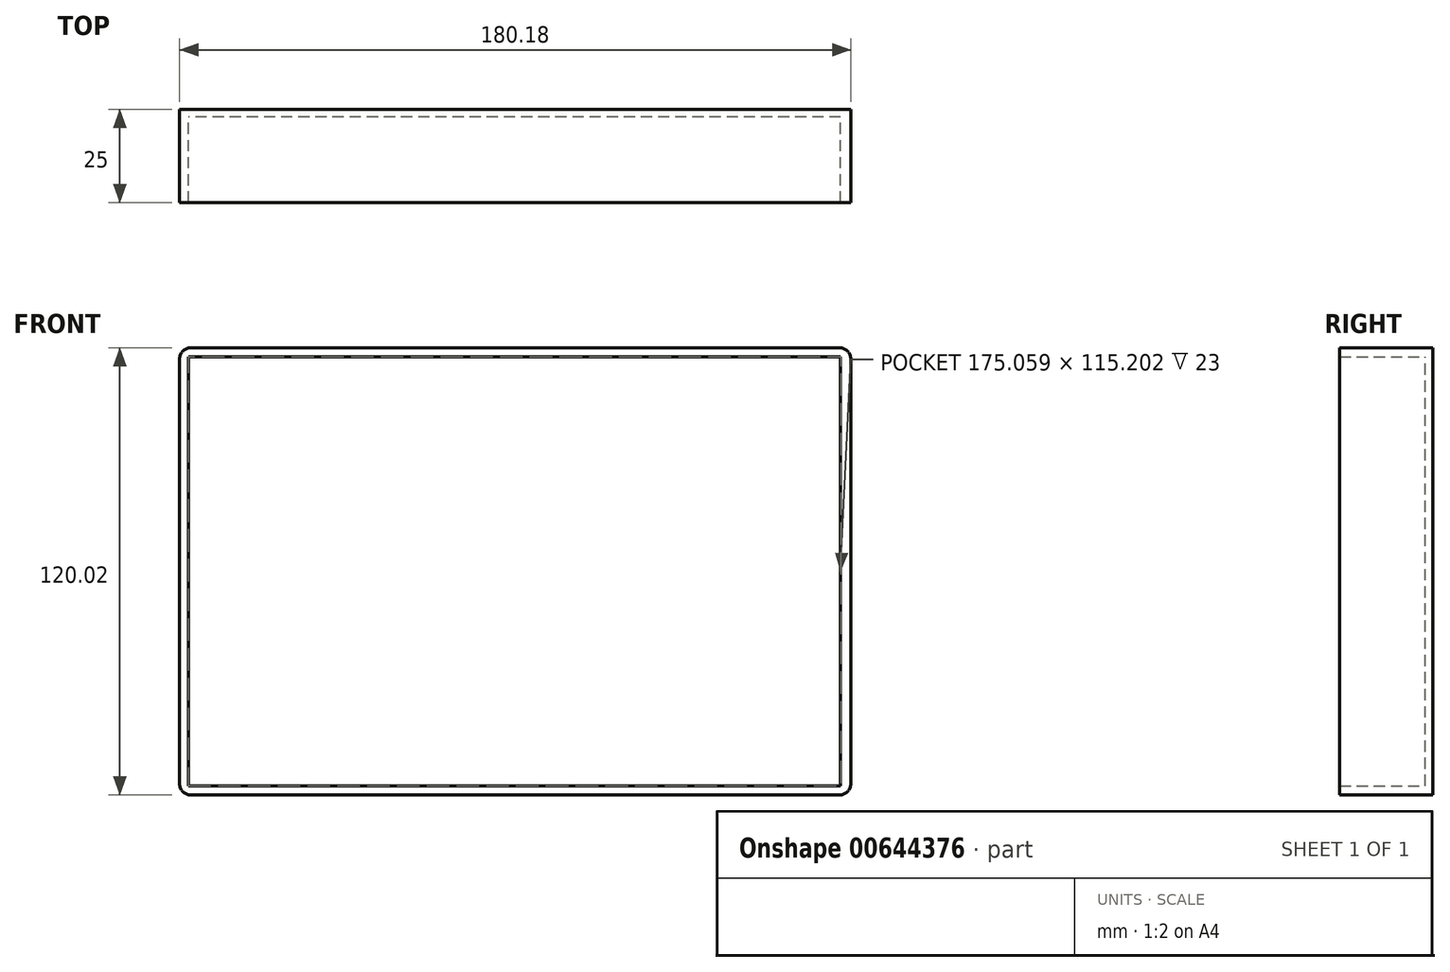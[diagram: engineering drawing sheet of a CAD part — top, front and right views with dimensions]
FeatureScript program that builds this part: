
annotation { "Feature Type Name" : "Feature", "Feature Type Description" : "" }
export const myFeature = defineFeature(function(context is Context, id is Id, definition is map)
    precondition{}
    {
        {
            var Q0;
            Q0=qCreatedBy(makeId("Front.planeOp"),FACE);
            var sketch = newSketch(context, id + "F0", { "sketchPlane" : qUnion([Q0])});
            skLineSegment(sketch, "E0.bottom", {"start": v(90.09, 60) * mm, "end": v(-90.09, 60) * mm});
            skLineSegment(sketch, "E0.top", {"start": v(90.09, -60) * mm, "end": v(-90.09, -60) * mm});
            skLineSegment(sketch, "E0.left", {"start": v(90.09, 60) * mm, "end": v(90.09, -60) * mm});
            skLineSegment(sketch, "E0.right", {"start": v(-90.09, 60) * mm, "end": v(-90.09, -60) * mm});
            skPoint(sketch, "E0.middle", {"position": v(0, 0) * mm});
            skLineSegment(sketch, "E1", {"start": v(-87.68, 57.6) * mm, "end": v(87.38, 57.6) * mm});
            skLineSegment(sketch, "E2", {"start": v(87.38, 57.6) * mm, "end": v(87.38, -57.6) * mm});
            skLineSegment(sketch, "E3", {"start": v(87.38, -57.6) * mm, "end": v(-87.68, -57.6) * mm});
            skLineSegment(sketch, "E4", {"start": v(-87.68, -57.6) * mm, "end": v(-87.68, 57.6) * mm});
            skLineSegment(sketch, "E5", {"start": v(-90.09, 60) * mm, "end": v(-87.68, 57.6) * mm});
            skLineSegment(sketch, "E6", {"start": v(0, 60) * mm, "end": v(0, 57.6) * mm});
            skPoint(sketch, "E6.endSnap0", {"position": v(-0.15, 57.6) * mm});
            skLineSegment(sketch, "E7", {"start": v(90.09, 60) * mm, "end": v(87.38, 57.6) * mm});
            skLineSegment(sketch, "E8", {"start": v(-90.09, 0) * mm, "end": v(-87.68, 0) * mm});
            skLineSegment(sketch, "E9", {"start": v(-87.68, -57.6) * mm, "end": v(-90.09, -60) * mm});
            skLineSegment(sketch, "E10", {"start": v(-0.15, -57.6) * mm, "end": v(-0.15, -60) * mm});
            skLineSegment(sketch, "E11", {"start": v(87.38, 0) * mm, "end": v(90.09, 0) * mm});
            skLineSegment(sketch, "E12", {"start": v(87.38, -57.6) * mm, "end": v(90.09, -60) * mm});
            skLineSegment(sketch, "E13", {"start": v(-87.68, 0) * mm, "end": v(0, 0) * mm});
            skLineSegment(sketch, "E14", {"start": v(0, 57.6) * mm, "end": v(0, 0) * mm});
            skLineSegment(sketch, "E15", {"start": v(0, 0) * mm, "end": v(87.38, 0) * mm});
            skLineSegment(sketch, "E16", {"start": v(0, 0) * mm, "end": v(-0.15, -57.6) * mm});
            skSolve(sketch);
        }
        {
            var Q0;
            {var subQ0=sQuery(id+"F0.wireOp",EDGE,"E5");Q0=makeQuery(id+"F0.imprint","IMPRINT",FACE,{"disambiguationData":[TD([[makeQuery(id+"F0.imprint","IMPRINT",EDGE,{"derivedFrom":subQ0}),1.0]])]});}
            extrude(context, id + "F1", {"entities" : qUnion([Q0]), "depth" : 25 * mm, "offsetDistance" : 25 * mm});
        }
        {
            var Q0;
            {var subQ2=sQuery(id+"F0.wireOp",EDGE,"E6");Q0=makeQuery(id+"F0.imprint","IMPRINT",FACE,{"disambiguationData":[TD([[makeQuery(id+"F0.imprint","IMPRINT",EDGE,{"derivedFrom":subQ2}),1.0]])]});}
            extrude(context, id + "F2", {"entities" : qUnion([Q0]), "operationType" : NewBodyOperationType.ADD, "depth" : 25 * mm, "offsetDistance" : 25 * mm});
        }
        {
            var Q0;
            {var subQ0=sQuery(id+"F0.wireOp",EDGE,"E5");Q0=makeQuery(id+"F0.imprint","IMPRINT",FACE,{"disambiguationData":[TD([[makeQuery(id+"F0.imprint","IMPRINT",EDGE,{"derivedFrom":subQ0}),-1.0]])]});}
            extrude(context, id + "F3", {"entities" : qUnion([Q0]), "operationType" : NewBodyOperationType.ADD, "depth" : 25 * mm, "offsetDistance" : 25 * mm});
        }
        {
            var Q0;
            {var subQ2=sQuery(id+"F0.wireOp",EDGE,"E8");Q0=makeQuery(id+"F0.imprint","IMPRINT",FACE,{"disambiguationData":[TD([[makeQuery(id+"F0.imprint","IMPRINT",EDGE,{"derivedFrom":subQ2}),-1.0]])]});}
            extrude(context, id + "F4", {"entities" : qUnion([Q0]), "operationType" : NewBodyOperationType.ADD, "depth" : 25 * mm, "offsetDistance" : 25 * mm});
        }
        {
            var Q0;
            {var subQ0=sQuery(id+"F0.wireOp",EDGE,"E9");Q0=makeQuery(id+"F0.imprint","IMPRINT",FACE,{"disambiguationData":[TD([[makeQuery(id+"F0.imprint","IMPRINT",EDGE,{"derivedFrom":subQ0}),1.0]])]});}
            extrude(context, id + "F5", {"entities" : qUnion([Q0]), "operationType" : NewBodyOperationType.ADD, "depth" : 25 * mm, "offsetDistance" : 25 * mm});
        }
        {
            var Q0;
            {var subQ2=sQuery(id+"F0.wireOp",EDGE,"E10");Q0=makeQuery(id+"F0.imprint","IMPRINT",FACE,{"disambiguationData":[TD([[makeQuery(id+"F0.imprint","IMPRINT",EDGE,{"derivedFrom":subQ2}),1.0]])]});}
            extrude(context, id + "F6", {"entities" : qUnion([Q0]), "operationType" : NewBodyOperationType.ADD, "depth" : 25 * mm, "offsetDistance" : 25 * mm});
        }
        {
            var Q0;
            {var subQ0=sQuery(id+"F0.wireOp",EDGE,"E7");Q0=makeQuery(id+"F0.imprint","IMPRINT",FACE,{"disambiguationData":[TD([[makeQuery(id+"F0.imprint","IMPRINT",EDGE,{"derivedFrom":subQ0}),1.0]])]});}
            extrude(context, id + "F7", {"entities" : qUnion([Q0]), "operationType" : NewBodyOperationType.ADD, "depth" : 25 * mm, "offsetDistance" : 25 * mm});
        }
        {
            var Q0;
            {var subQ2=sQuery(id+"F0.wireOp",EDGE,"E11");Q0=makeQuery(id+"F0.imprint","IMPRINT",FACE,{"disambiguationData":[TD([[makeQuery(id+"F0.imprint","IMPRINT",EDGE,{"derivedFrom":subQ2}),-1.0]])]});}
            extrude(context, id + "F8", {"entities" : qUnion([Q0]), "operationType" : NewBodyOperationType.ADD, "depth" : 25 * mm, "offsetDistance" : 25 * mm});
        }
        {
            var Q0;
            {var subQ4=sQuery(id+"F0.wireOp",EDGE,"E13");Q0=makeQuery(id+"F0.imprint","IMPRINT",FACE,{"disambiguationData":[TD([[makeQuery(id+"F0.imprint","IMPRINT",EDGE,{"derivedFrom":subQ4}),1.0]])]});}
            var Q1;
            {var subQ3=sQuery(id+"F0.wireOp",EDGE,"E14");Q1=makeQuery(id+"F0.imprint","IMPRINT",FACE,{"disambiguationData":[TD([[makeQuery(id+"F0.imprint","IMPRINT",EDGE,{"derivedFrom":subQ3}),1.0]])]});}
            extrude(context, id + "F9", {"entities" : qUnion([Q0, Q1]), "operationType" : NewBodyOperationType.ADD, "depth" : 2 * mm, "offsetDistance" : 25 * mm});
        }
        {
            var Q0;
            {var subQ3=sQuery(id+"F0.wireOp",EDGE,"E14");Q0=makeQuery(id+"F0.imprint","IMPRINT",FACE,{"disambiguationData":[TD([[makeQuery(id+"F0.imprint","IMPRINT",EDGE,{"derivedFrom":subQ3}),1.0]])]});}
            extrude(context, id + "F10", {"entities" : qUnion([Q0]), "operationType" : NewBodyOperationType.ADD, "depth" : 2 * mm, "offsetDistance" : 25 * mm});
        }
        {
            var Q0;
            {var subQ4=sQuery(id+"F0.wireOp",EDGE,"E13");Q0=makeQuery(id+"F0.imprint","IMPRINT",FACE,{"disambiguationData":[TD([[makeQuery(id+"F0.imprint","IMPRINT",EDGE,{"derivedFrom":subQ4}),-1.0]])]});}
            extrude(context, id + "F11", {"entities" : qUnion([Q0]), "operationType" : NewBodyOperationType.ADD, "depth" : 2 * mm, "offsetDistance" : 25 * mm});
        }
        {
            var Q0;
            {var subQ3=sQuery(id+"F0.wireOp",EDGE,"E15");Q0=makeQuery(id+"F0.imprint","IMPRINT",FACE,{"disambiguationData":[TD([[makeQuery(id+"F0.imprint","IMPRINT",EDGE,{"derivedFrom":subQ3}),-1.0]])]});}
            extrude(context, id + "F12", {"entities" : qUnion([Q0]), "operationType" : NewBodyOperationType.ADD, "depth" : 2 * mm, "offsetDistance" : 25 * mm});
        }
        {
            var Q0;
            {var subQ0=sQuery(id+"F0.wireOp",EDGE,"E5");var subQ1=sQuery(id+"F0.wireOp",EDGE,"E0.right");var subQ2=sQuery(id+"F0.wireOp",EDGE,"E0.bottom");Q0=makeQuery(id+"F3.boolean.opBoolean","MERGE",EDGE,{"derivedFrom":[makeQuery(id+"F1.opExtrude","SWEPT_EDGE",EDGE,{"disambiguationData":[OSD([subQ2,subQ1,subQ0])]}),makeQuery(id+"F3.opExtrude","SWEPT_EDGE",EDGE,{"disambiguationData":[OSD([subQ2,subQ1,subQ0])]})]});}
            fillet(context, id + "F13", {"entities" : qUnion([Q0]), "radius" : 3 * mm, "tangentPropagation" : true, "allowEdgeOverflow" : false});
        }
        {
            var Q0;
            {var subQ0=sQuery(id+"F0.wireOp",EDGE,"E7");var subQ1=sQuery(id+"F0.wireOp",EDGE,"E0.left");var subQ2=sQuery(id+"F0.wireOp",EDGE,"E0.bottom");Q0=makeQuery(id+"F7.boolean.opBoolean","MERGE",EDGE,{"derivedFrom":[makeQuery(id+"F2.opExtrude","SWEPT_EDGE",EDGE,{"disambiguationData":[OSD([subQ2,subQ1,subQ0])]}),makeQuery(id+"F7.opExtrude","SWEPT_EDGE",EDGE,{"disambiguationData":[OSD([subQ2,subQ1,subQ0])]})]});}
            fillet(context, id + "F14", {"entities" : qUnion([Q0]), "radius" : 3 * mm, "tangentPropagation" : true, "allowEdgeOverflow" : false});
        }
        {
            var Q0;
            {var subQ0=sQuery(id+"F0.wireOp",EDGE,"E12");var subQ1=sQuery(id+"F0.wireOp",EDGE,"E0.left");var subQ2=sQuery(id+"F0.wireOp",EDGE,"E0.top");Q0=makeQuery(id+"F8.boolean.opBoolean","MERGE",EDGE,{"derivedFrom":[makeQuery(id+"F6.opExtrude","SWEPT_EDGE",EDGE,{"disambiguationData":[OSD([subQ2,subQ1,subQ0])]}),makeQuery(id+"F8.opExtrude","SWEPT_EDGE",EDGE,{"disambiguationData":[OSD([subQ2,subQ1,subQ0])]})]});}
            fillet(context, id + "F15", {"entities" : qUnion([Q0]), "radius" : 3 * mm, "tangentPropagation" : true, "allowEdgeOverflow" : false});
        }
        {
            var Q0;
            {var subQ0=sQuery(id+"F0.wireOp",EDGE,"E9");var subQ1=sQuery(id+"F0.wireOp",EDGE,"E0.right");var subQ2=sQuery(id+"F0.wireOp",EDGE,"E0.top");Q0=makeQuery(id+"F5.boolean.opBoolean","MERGE",EDGE,{"derivedFrom":[makeQuery(id+"F4.opExtrude","SWEPT_EDGE",EDGE,{"disambiguationData":[OSD([subQ2,subQ1,subQ0])]}),makeQuery(id+"F5.opExtrude","SWEPT_EDGE",EDGE,{"disambiguationData":[OSD([subQ2,subQ1,subQ0])]})]});}
            fillet(context, id + "F16", {"entities" : qUnion([Q0]), "radius" : 3 * mm, "tangentPropagation" : true, "allowEdgeOverflow" : false});
        }
    });
